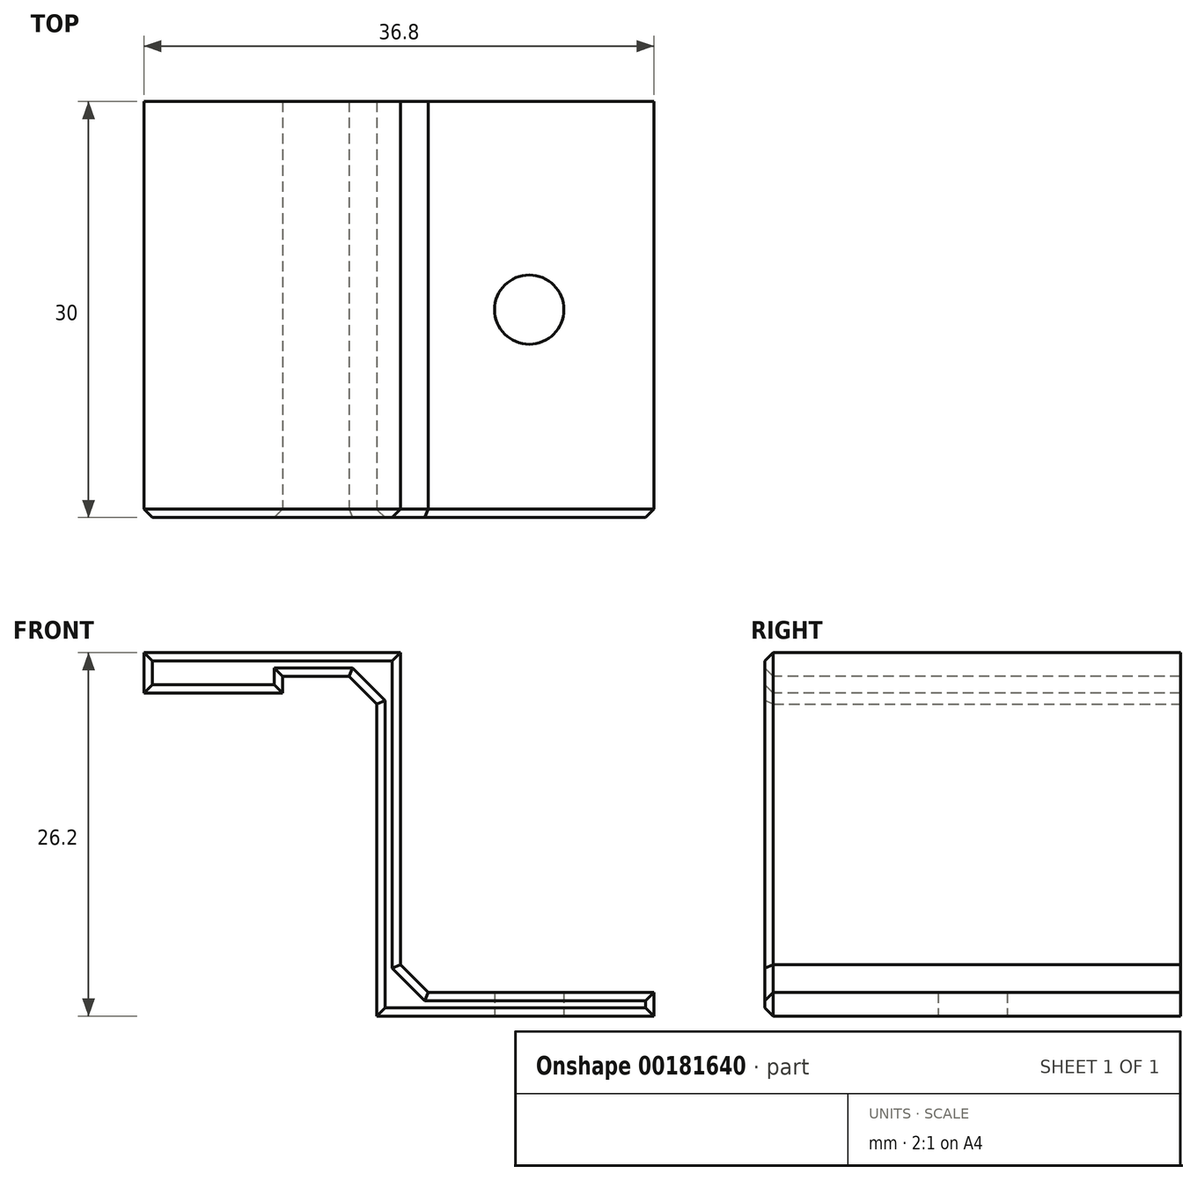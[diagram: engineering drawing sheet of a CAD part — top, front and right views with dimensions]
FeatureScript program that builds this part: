
annotation { "Feature Type Name" : "Feature", "Feature Type Description" : "" }
export const myFeature = defineFeature(function(context is Context, id is Id, definition is map)
    precondition{}
    {
        {
            var Q0;
            Q0=qCreatedBy(makeId("Front.planeOp"),FACE);
            var sketch = newSketch(context, id + "F0", { "sketchPlane" : qUnion([Q0])});
            skLineSegment(sketch, "E0", {"start": v(0, 0) * mm, "end": v(20, 0) * mm});
            skLineSegment(sketch, "E1", {"start": v(20, 0) * mm, "end": v(20, 1.7) * mm});
            skLineSegment(sketch, "E2", {"start": v(20, 1.7) * mm, "end": v(1.7, 1.7) * mm});
            skLineSegment(sketch, "E3", {"start": v(1.7, 1.7) * mm, "end": v(1.7, 26.2) * mm});
            skLineSegment(sketch, "E4", {"start": v(1.7, 26.2) * mm, "end": v(-16.8, 26.2) * mm});
            skLineSegment(sketch, "E5", {"start": v(-16.8, 26.2) * mm, "end": v(-16.8, 23.3) * mm});
            skLineSegment(sketch, "E6", {"start": v(0, 24.5) * mm, "end": v(0, 0) * mm});
            skLineSegment(sketch, "E7", {"start": v(0, 24.5) * mm, "end": v(-6.8, 24.5) * mm});
            skLineSegment(sketch, "E8", {"start": v(-6.8, 24.5) * mm, "end": v(-6.8, 23.3) * mm});
            skLineSegment(sketch, "E9", {"start": v(-6.8, 23.3) * mm, "end": v(-16.8, 23.3) * mm});
            skSolve(sketch);
        }
        {
            var Q0;
            Q0=makeQuery(id+"F0.imprint","IMPRINT",FACE,{"disambiguationData":[TD([[makeQuery(id+"F0.imprint","IMPRINT",EDGE,{"derivedFrom":sQuery(id+"F0.wireOp",EDGE,"E0")}),1.0]])]});
            extrude(context, id + "F1", {"entities" : qUnion([Q0]), "oppositeDirection" : true, "depth" : 30 * mm});
        }
        {
            var Q0;
            Q0=makeQuery(id+"F1.opExtrude","SWEPT_EDGE",EDGE,{"disambiguationData":[OSD([sQuery(id+"F0.wireOp",EDGE,"E2"),sQuery(id+"F0.wireOp",EDGE,"E3")])]});
            var Q1;
            Q1=makeQuery(id+"F1.opExtrude","SWEPT_EDGE",EDGE,{"disambiguationData":[OSD([sQuery(id+"F0.wireOp",EDGE,"E6"),sQuery(id+"F0.wireOp",EDGE,"E7")])]});
            chamfer(context, id + "F2", {"entities" : qUnion([Q0, Q1]), "width" : 2 * mm, "tangentPropagation" : true});
        }
        {
            var Q0;
            Q0=makeQuery(id+"F1.opExtrude","CAP_FACE",FACE,{"disambiguationData":[OSD([sQuery(id+"F0.wireOp",EDGE,"E0"),sQuery(id+"F0.wireOp",EDGE,"E1"),sQuery(id+"F0.wireOp",EDGE,"E2"),sQuery(id+"F0.wireOp",EDGE,"E3"),sQuery(id+"F0.wireOp",EDGE,"E4"),sQuery(id+"F0.wireOp",EDGE,"E5"),sQuery(id+"F0.wireOp",EDGE,"E6"),sQuery(id+"F0.wireOp",EDGE,"E7"),sQuery(id+"F0.wireOp",EDGE,"E8"),sQuery(id+"F0.wireOp",EDGE,"E9")])],"isStart":true});
            chamfer(context, id + "F3", {"entities" : qUnion([Q0]), "width" : .6 * mm, "tangentPropagation" : true});
        }
        {
            var Q0;
            Q0=makeQuery(id+"F1.opExtrude","SWEPT_FACE",FACE,{"disambiguationData":[OSD([sQuery(id+"F0.wireOp",EDGE,"E0")])]});
            var sketch = newSketch(context, id + "F4", { "sketchPlane" : qUnion([Q0])});
            skCircle(sketch, "E10", {"center": v(11, -15) * mm, "radius": 2.5 * mm});
            skSolve(sketch);
        }
        {
            var Q0;
            Q0=makeQuery(id+"F4.imprint","IMPRINT",FACE,{"disambiguationData":[TD([[makeQuery(id+"F4.imprint","IMPRINT",EDGE,{"derivedFrom":sQuery(id+"F4.wireOp",EDGE,"E10")}),1.0]])]});
            var Q1;
            Q1=makeQuery(id+"F1.opExtrude","SWEPT_FACE",FACE,{"disambiguationData":[OSD([sQuery(id+"F0.wireOp",EDGE,"E2")])]});
            extrude(context, id + "F5", {"entities" : qUnion([Q0]), "operationType" : NewBodyOperationType.REMOVE, "endBound" : BoundingType.UP_TO_SURFACE, "oppositeDirection" : true, "endBoundEntityFace" : qUnion([Q1]), "depth" : 25 * mm});
        }
    });
